# Revit family: P350169-143
name_source: partatom
category: Lighting Fixtures
units: mm (PartAtom-declared; Revit-internal decimal feet)

## family parameters
Cut with Voids When Loaded = No
Host = Face
Light Source = No
OmniClass Number = 23.80.70.11.14.17
OmniClass Title = Direct/Indirect
Part Type = Normal
Room Calculation Point = No
Round Connector Dimension = Use Diameter
Shared = Yes

## types (1)
- P350169-143
    Apparent Load = 60 VA
    Assembly Code = D5020200
    Connector Description = Lighting Connector
    Default Elevation = 48 "
    Description = Gulliver Collection Two-Light Graphite and Weathered Gray Farmhouse Style Flush Mount Ceiling Light
    Features = Application: Ideal for any hallway, stairwell, entryway, closet, pantry, kitchen, or sitting room.
Style: Perfect for coastal or farmhouse style settings.
Finish: The circular bands are constructed from a faux-wood coated in a weathered gray finish accented by a graphite ceiling plate and metal details for perfect modern rustic character.
Materials: Constructed from steel to ensure a long product lifespan.
Glass: Light sources exude a comforting country glow as they peek through the circular bands of the open-cage design.
Bulbs: For ideal illumination, use 2 medium base bulbs that are sold separately (60w max - LED/CFL/incandescent). Compatible with dimmable bulbs.
Dimensions: Measures 14.37-inch width by 6.5-inch height.
Certifications: cETLus damp location listed.
Pairs With: Pairs with Progress Lighting fixtures from the Briarwood, Mast, and Hemsworth collections.
Warranty: Our 1-Year Limited Warranty guarantees your complete satisfaction with your purchase and includes professional after-sales customer service support. Make your purchase today to breathe new life into your lighting design!
    Fixture distribution = Direct
    Glass = Paint - Hubbell - White Texture
    Gold = Hubbell - Gold
    Housing Material = Paint - Hubbell - Textured Camera Black
    Lamp = LED/CFL/incandescent
    Load Classification = Lighting
    Manufacturer = Progress Lighting
    Model = P350169-143
    Power Factor = 1
    Product Documentation Link = https://hubbellcdn.com
    Product Link = https://www.hubbell.com
    URL = https://www.hubbell.com
    Voltage = 120 V
    Warranty = 1 year Warranty
    Wattage Comments = 60W
    Watts = 60 W
    Widh = 14.37 "
    Wood = Hubbell Gray

## geometry (parser evidence)
native form markers: Sweep x7
no freeform markers — native parametric forms only
